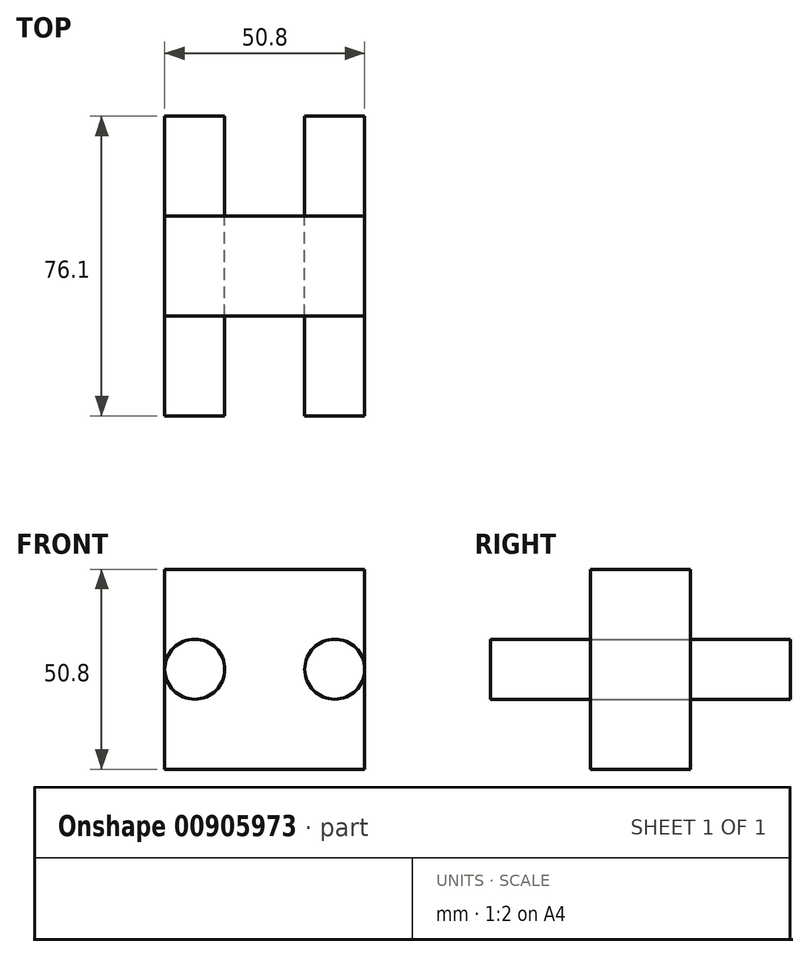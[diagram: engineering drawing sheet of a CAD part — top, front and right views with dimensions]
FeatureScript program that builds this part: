
annotation { "Feature Type Name" : "Feature", "Feature Type Description" : "" }
export const myFeature = defineFeature(function(context is Context, id is Id, definition is map)
    precondition{}
    {
        {
            var Q0;
            Q0=qCreatedBy(makeId("Front.planeOp"),FACE);
            var sketch = newSketch(context, id + "F0", { "sketchPlane" : qUnion([Q0])});
            skLineSegment(sketch, "E0", {"start": v(0, 25.4) * mm, "end": v(25.4, 25.4) * mm});
            skLineSegment(sketch, "E1", {"start": v(25.4, 25.4) * mm, "end": v(25.4, 0) * mm});
            skLineSegment(sketch, "E2", {"start": v(25.4, 0) * mm, "end": v(25.4, -25.4) * mm});
            skLineSegment(sketch, "E3", {"start": v(25.4, -25.4) * mm, "end": v(0, -25.4) * mm});
            skLineSegment(sketch, "E4", {"start": v(0, -25.4) * mm, "end": v(-25.4, -25.4) * mm});
            skLineSegment(sketch, "E5", {"start": v(-25.4, -25.4) * mm, "end": v(-25.4, 0) * mm});
            skLineSegment(sketch, "E6", {"start": v(0, 25.4) * mm, "end": v(-25.4, 25.4) * mm});
            skLineSegment(sketch, "E7", {"start": v(-25.4, 25.4) * mm, "end": v(-25.4, 0) * mm});
            skCircle(sketch, "E8", {"center": v(17.78, 0) * mm, "radius": 7.62 * mm});
            skCircle(sketch, "E9", {"center": v(-17.78, 0) * mm, "radius": 7.62 * mm});
            skSolve(sketch);
        }
        {
            var Q0;
            Q0=makeQuery(id+"F0.imprint","IMPRINT",FACE,{"disambiguationData":[TD([[makeQuery(id+"F0.imprint","IMPRINT",EDGE,{"derivedFrom":sQuery(id+"F0.wireOp",EDGE,"E8")}),1.0]])]});
            var Q1;
            Q1=makeQuery(id+"F0.imprint","IMPRINT",FACE,{"disambiguationData":[TD([[makeQuery(id+"F0.imprint","IMPRINT",EDGE,{"derivedFrom":sQuery(id+"F0.wireOp",EDGE,"E9")}),1.0]])]});
            extrude(context, id + "F1", {"entities" : qUnion([Q0, Q1]), "oppositeDirection" : true, "depth" : 25.4 * mm, "offsetDistance" : 25.4 * mm});
        }
        {
            var Q0;
            Q0 = qSketchRegion(id + "F0", true);
            extrude(context, id + "F2", {"entities" : qUnion([Q0]), "depth" : 25.4 * mm, "offsetDistance" : 25.4 * mm});
        }
        {
            var Q0;
            Q0=makeQuery(id+"F1.opExtrude","CAP_FACE",FACE,{"disambiguationData":[OSD([sQuery(id+"F0.wireOp",EDGE,"E8")])],"isStart":false});
            var Q1;
            Q1=makeQuery(id+"F1.opExtrude","CAP_FACE",FACE,{"disambiguationData":[OSD([sQuery(id+"F0.wireOp",EDGE,"E9")])],"isStart":false});
            extrude(context, id + "F3", {"entities" : qUnion([Q0, Q1]), "oppositeDirection" : true, "depth" : 76.1 * mm, "offsetDistance" : 25.4 * mm});
        }
    });
